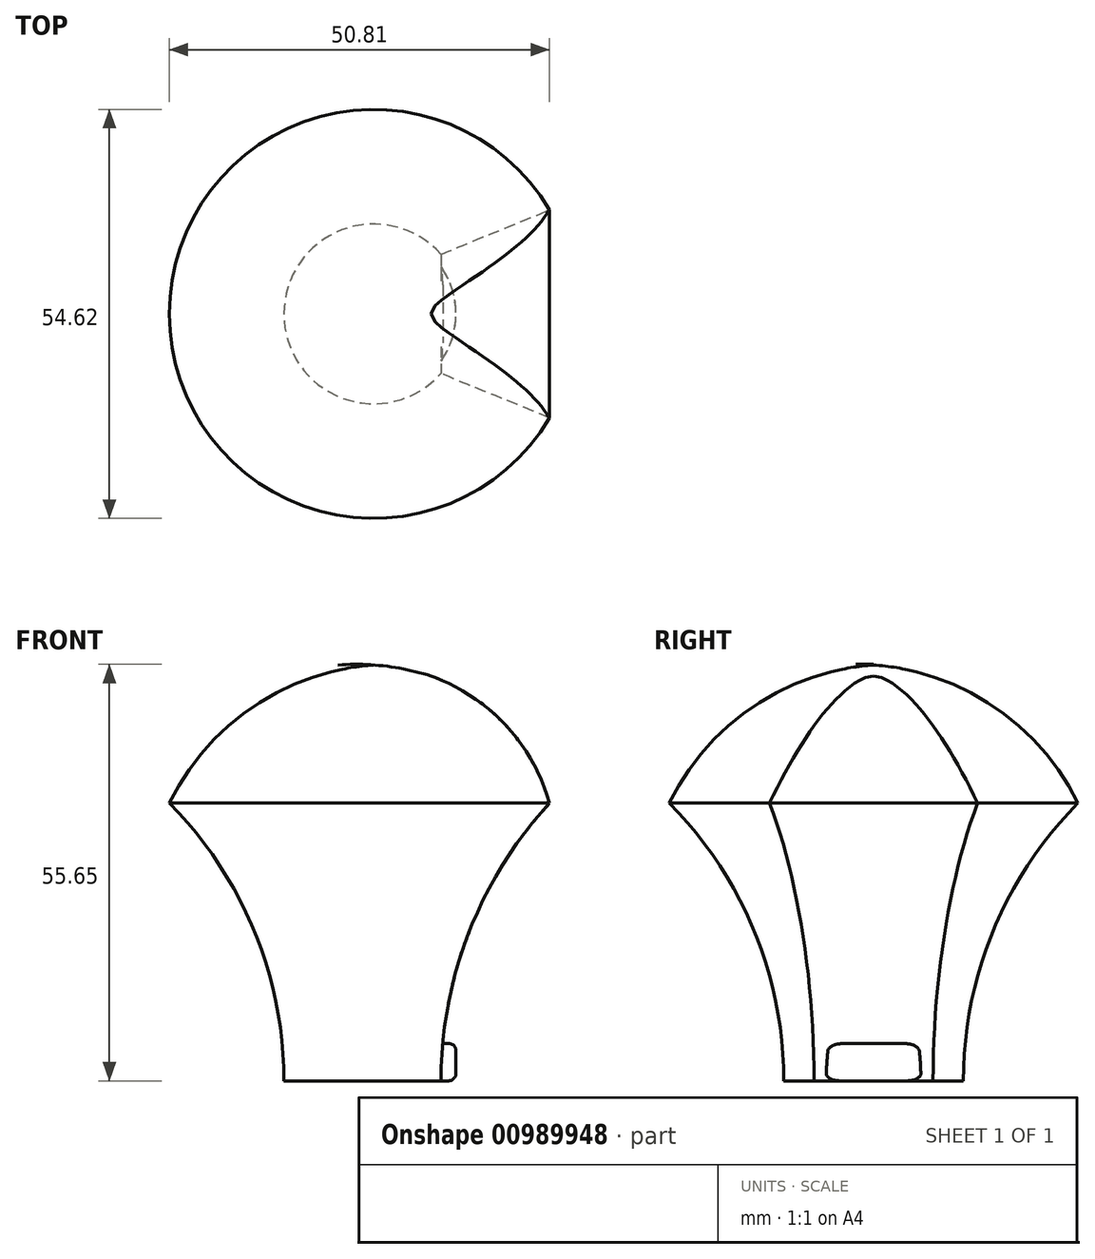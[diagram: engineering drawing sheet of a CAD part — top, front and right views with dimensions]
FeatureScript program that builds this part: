
annotation { "Feature Type Name" : "Feature", "Feature Type Description" : "" }
export const myFeature = defineFeature(function(context is Context, id is Id, definition is map)
    precondition{}
    {
        {
            var Q0;
            Q0=qCreatedBy(makeId("Front.planeOp"),FACE);
            var sketch = newSketch(context, id + "F0", { "sketchPlane" : qUnion([Q0])});
            skLineSegment(sketch, "E0.bottom", {"start": v(0, 0) * mm, "end": v(-12, 0) * mm});
            skLineSegment(sketch, "E0.left", {"start": v(0, 0) * mm, "end": v(0, 55.56) * mm});
            skArc(sketch, "E1", {"start": v(0, 55.56) * mm, "mid": v(-16.12, 49.98) * mm, "end": v(-27.3, 37.1) * mm});
            skArc(sketch, "E2", {"start": v(-12, 0) * mm, "mid": v(-15.98, 20.06) * mm, "end": v(-27.3, 37.1) * mm});
            skPoint(sketch, "E3.orphan", {"position": v(-24, 0) * mm});
            skSolve(sketch);
        }
        {
            var Q0;
            Q0=makeQuery(id+"F0.imprint","IMPRINT",FACE,{"disambiguationData":[TD([[makeQuery(id+"F0.imprint","IMPRINT",EDGE,{"derivedFrom":sQuery(id+"F0.wireOp",EDGE,"E0.bottom")}),-1.0]])]});
            var Q1;
            Q1=sQuery(id+"F0.wireOp",EDGE,"E0.left");
            revolve(context, id + "F1", {"surfaceOperationType" : NewSurfaceOperationType.NEW, "entities" : qUnion([Q0]), "axis" : qUnion([Q1]), "revolveType" : RevolveType.FULL});
        }
        {
            var Q0;
            Q0=qCreatedBy(makeId("Front.planeOp"),FACE);
            var sketch = newSketch(context, id + "F2", { "sketchPlane" : qUnion([Q0])});
            skArc(sketch, "E4", {"start": v(23.5, 37.1) * mm, "mid": v(12.75, 19.91) * mm, "end": v(9, 0) * mm});
            skArc(sketch, "E5", {"start": v(23.5, 37.1) * mm, "mid": v(14.76, 50.16) * mm, "end": v(0, 55.56) * mm});
            skLineSegment(sketch, "E6", {"start": v(0, 55.56) * mm, "end": v(27.93, 54.56) * mm});
            skLineSegment(sketch, "E7", {"start": v(27.93, 54.56) * mm, "end": v(27.93, 0) * mm});
            skLineSegment(sketch, "E8", {"start": v(27.93, 0) * mm, "end": v(9, 0) * mm});
            skSolve(sketch);
        }
        {
            var Q0;
            Q0=makeQuery(id+"F2.imprint","IMPRINT",FACE,{"disambiguationData":[TD([[makeQuery(id+"F2.imprint","IMPRINT",EDGE,{"derivedFrom":sQuery(id+"F2.wireOp",EDGE,"E4")}),1.0]])]});
            extrude(context, id + "F3", {"entities" : qUnion([Q0]), "operationType" : NewBodyOperationType.REMOVE, "endBound" : BoundingType.SYMMETRIC, "oppositeDirection" : true, "depth" : 30 * mm, "offsetDistance" : 25 * mm});
        }
        {
            var Q0;
            Q0=qCreatedBy(makeId("Top.planeOp"),FACE);
            var sketch = newSketch(context, id + "F4", { "sketchPlane" : qUnion([Q0])});
            skCircle(sketch, "E9", {"center": v(0, 0) * mm, "radius": 11 * mm});
            skSolve(sketch);
        }
        {
            var Q0;
            Q0 = qSketchRegion(id + "F4", true);
            extrude(context, id + "F5", {"entities" : qUnion([Q0]), "operationType" : NewBodyOperationType.ADD, "depth" : 5 * mm, "offsetDistance" : 25 * mm});
        }
        {
            var Q0;
            Q0=makeQuery(id+"F5.opExtrude","CAP_EDGE",EDGE,{"disambiguationData":[OSD([sQuery(id+"F4.wireOp",EDGE,"E9")])],"isStart":false});
            var Q1;
            Q1=makeQuery(id+"F5.opExtrude","CAP_EDGE",EDGE,{"disambiguationData":[OSD([sQuery(id+"F4.wireOp",EDGE,"E9")])],"isStart":true});
            fillet(context, id + "F6", {"entities" : qUnion([Q0, Q1]), "tangentPropagation" : true, "radius" : 1 * mm, "defaultsChanged" : true, "vertexSettings" : [], "allowEdgeOverflow" : false});
        }
    });
